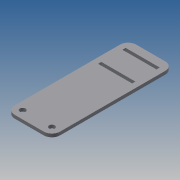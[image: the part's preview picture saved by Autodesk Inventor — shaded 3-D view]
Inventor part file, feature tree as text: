
AUTODESK INVENTOR PART (.ipt)
format: ipt  version: 2013 (Build 170138000, 138)  size: 131,072 bytes
history: native  units: mm
features: extrude x4, sketch x4, fillet x2, pattern_linear x1, projected_geometry x1
ambient origin geometry x8: Origin, YZ Plane, XZ Plane, XY Plane, X Axis, Y Axis, Z Axis, Center Point
bodies: Solid1 (feature_tree)
feature tree (12):
  extrude  "Extrusion1"  Depth=28.0mm
  extrude  "Extrusion4"  Depth=3.5mm
  fillet  "Fillet2"  Radius=18.0mm
  extrude  "Extrusion2"  Depth=10.0mm
  extrude  "Extrusion3"  Depth=2.0mm TaperAngle=0.0deg
  pattern_linear  "Rectangular Pattern1"  Spacing1=1.0mm  [1 undecoded]
  fillet  "Fillet1"  Radius=20.0mm
  sketch  "Sketch1"  dims[d0=75.0mm d2=28.0mm]
  sketch  "Sketch2"  dims[d3=5.0mm d4=3.5mm d5=18.0mm]
  sketch  "Sketch3"  dims[d6=2.0mm d7=0.0mm d8=10.0mm]
  projected_geometry  "Projected Loop1"
  sketch  "Sketch4"  dims[d10=22.0mm d11=2.0mm d12=0.0mm d13=1.0mm d14=0.0mm d15=20.0mm d17=50.0mm d18=3.0mm d19=21.0mm d21=2.0mm d22=5.0mm d23=15.0mm d24=1.0mm d25=0.0mm d26=5.0mm]
note: 1 required parameter value undecoded (feature->parameter linkage not recoverable at this tier; creation-order binding heuristic only, values carry confidence <= 0.55)
